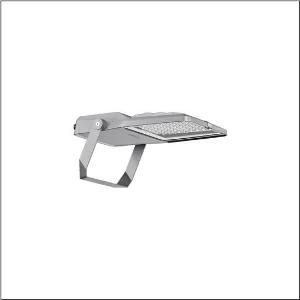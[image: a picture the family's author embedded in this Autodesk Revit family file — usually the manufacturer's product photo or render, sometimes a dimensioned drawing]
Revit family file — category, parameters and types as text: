
# Revit family: floodlight_fl_21_iq_mini___pl43_5xa7772d4a1a_cd74
name_source: partatom
category: Lighting Fixtures
units: mm (PartAtom-declared; Revit-internal decimal feet)

## family parameters
Cut with Voids When Loaded = No
Host = Face
Light Source = No
Part Type = Normal
Room Calculation Point = No
Round Connector Dimension = Use Diameter
Shared = No

## types (1)
- --- (1 x LED, 19090 lm, 143 W, 4000K)
    Apparent Load = 143 VA
    CIE Flux Codes = 27 78 99 100 100
    Color Rendering = 70
    Color Temperature = 4000K
    Default Elevation = 1800 mm
    Description = Floodlight FL 21 iQ mini, floodlight, primary light control with lens, of PMMA, primary optical cover: protective disc, of toughened safety glass, transparent, light distribution: PL43, light emission: direct distribution, installation type: surface-mounted, LED, High Power LED, rated luminous flux: 19.090lm, luminous efficacy: 134lm/W, light colour: 740, colour temperature: 4000K, control: Street-Remote, Auto-Match, Temp-Guard, Night-Set, Smart-Wire, Desk-Remote (wireless, voltage-free reading and setting of iQ features in the workshop via application-optimized NFC function/RFID function), optimised constant luminous flux control (CLO 2.0), with terminal, 6-pole, mains connection: 220..240V, AC, 50/60Hz, start of lifetime: 143W, end of service life: 152W, reduction: 61W, luminaire housing, of diecast aluminium, powder-coated, Siteco® metallic grey (DB 702S), corrosivity category C5 mid according to DIN EN ISO 12944, sealing non-destructively replaceable, mounting bracket, of steel, galvanised, powder-coated, Siteco® metallic grey (DB 702S), protection rating (complete): IP66, insulation class (complete): insulation class II (safety insulation), certification: CE, ENEC, VDE, protection symbol: D, impact resistance: IK08, permissible operating ambient temperature: -40..+40°C, permissible operating ambient temperature for outdoor applications: -40..+50°C, standard: DIN EN 12944, LABS conformity tested according to VDMA 24364:2018-05, packaging unit: 1 piece

Light Distribution: PL43
    Height = 70 mm
    Lamp = 1 x LED
    Lamp Light Flux = 19090 lm
    Lamp Power = 143 W
    Lamp count = 1
    Length = 485 mm
    Luminous efficacy = 133 lm/W
    Manufacturer = Siteco
    ModVariant = No
    Model = 5XA7772D4A1A
    Number of Poles = 1
    OnlyDefault = Yes
    Power Factor = 1
    Product Name = Floodlight FL 21 iQ mini | PL43
    Product group = floodlight | pylon annexe
    ProductGroupID = 6200
    Protection Class = Protection class II
    Protection Degree = IP 66
    RLX_Detail_Level = 1
    RLX_Emergency_Light_Flux = 0 lm
    RLX_Emergency_Type = 0
    RLX_Emergency_Type_DB = No
    RlxData = <blob elided: 96389 chars, md5=092ddea9>
    Socket = socket
    Standby Power = 0 W
    System Light Flux = 19090 lm
    System Power = 143 W
    Type Comments = factory setting: luminous flux: 100 % | dim-lin: 254 | 730 mA
    Type Image = l_1006845.jpg
    URL = http://relux.com
    VarID = @adj_093659
    Voltage = 0 V
    Weight = 0.00 kg
    Width = 337 mm

## geometry (parser evidence)
native form markers: Blend x4, Sweep x11
no freeform markers — native parametric forms only
